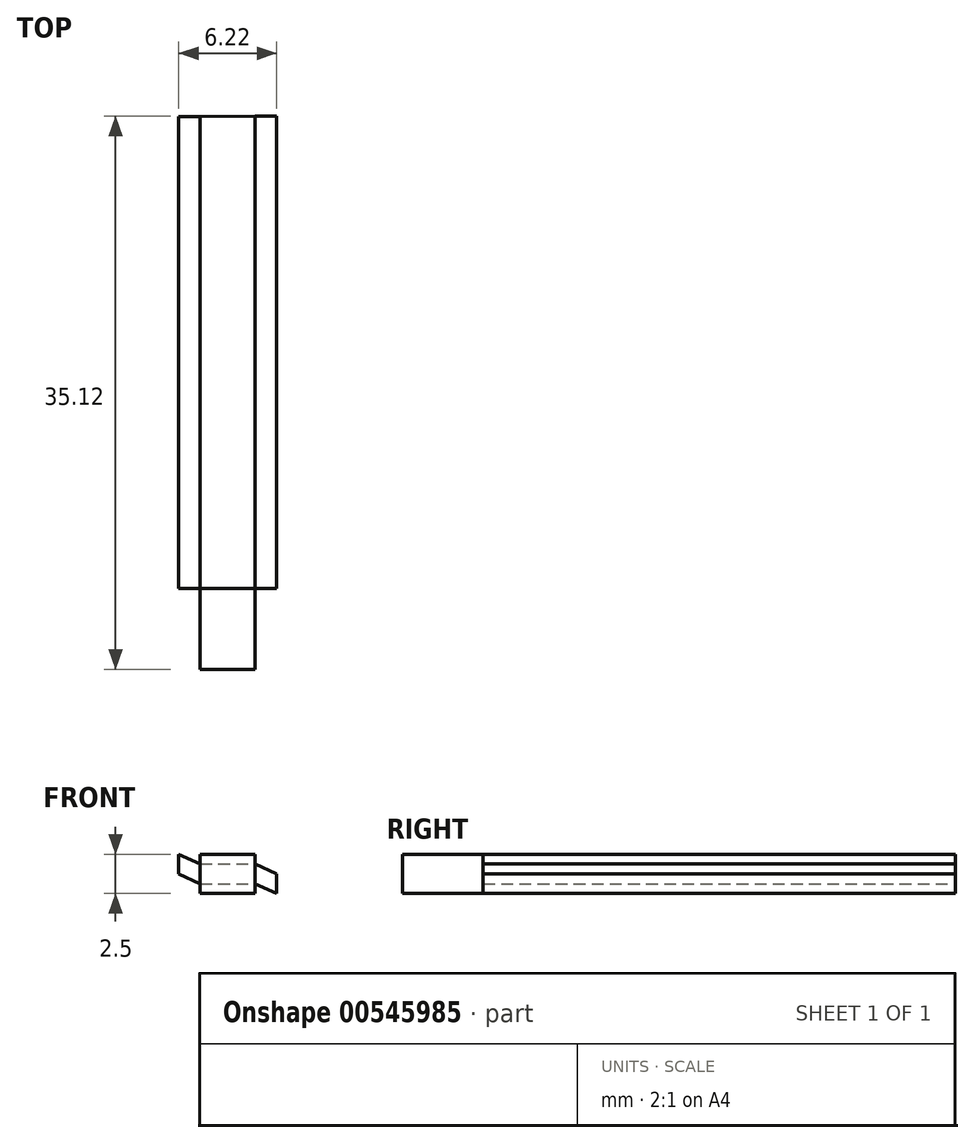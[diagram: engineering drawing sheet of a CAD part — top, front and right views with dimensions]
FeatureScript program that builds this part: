
annotation { "Feature Type Name" : "Feature", "Feature Type Description" : "" }
export const myFeature = defineFeature(function(context is Context, id is Id, definition is map)
    precondition{}
    {
        {
            var Q0;
            Q0=qCreatedBy(makeId("Top.planeOp"),FACE);
            var sketch = newSketch(context, id + "F0", { "sketchPlane" : qUnion([Q0])});
            skLineSegment(sketch, "E0", {"start": v(-3.25, 0) * mm, "end": v(3.25, 0) * mm});
            skLineSegment(sketch, "E1", {"start": v(-1.75, 0) * mm, "end": v(-1.75, -5.12) * mm});
            skLineSegment(sketch, "E2", {"start": v(-1.75, -5.12) * mm, "end": v(1.75, -5.12) * mm});
            skLineSegment(sketch, "E3", {"start": v(1.75, -5.12) * mm, "end": v(1.75, 0) * mm});
            skPoint(sketch, "E4", {"position": v(0, -5.12) * mm});
            skLineSegment(sketch, "E5", {"start": v(1.75, 0) * mm, "end": v(1.75, 30) * mm});
            skLineSegment(sketch, "E6", {"start": v(-1.75, 0) * mm, "end": v(-1.75, 29.98) * mm});
            skLineSegment(sketch, "E7", {"start": v(-1.75, 29.98) * mm, "end": v(1.75, 30) * mm});
            skSolve(sketch);
        }
        {
            var Q0;
            {var subQ2=sQuery(id+"F0.wireOp",EDGE,"E5");Q0=makeQuery(id+"F0.imprint","IMPRINT",FACE,{"disambiguationData":[TD([[makeQuery(id+"F0.imprint","IMPRINT",EDGE,{"derivedFrom":subQ2}),1.0]])]});}
            extrude(context, id + "F1", {"entities" : qUnion([Q0]), "depth" : 0.62 * mm, "offsetDistance" : 25 * mm, "hasSecondDirection" : true, "secondDirectionOppositeDirection" : true, "secondDirectionDepth" : 0.62 * mm});
        }
        {
            var Q0;
            Q0=qCreatedBy(makeId("Front.planeOp"),FACE);
            var sketch = newSketch(context, id + "F2", { "sketchPlane" : qUnion([Q0])});
            skLineSegment(sketch, "E8.bottom", {"start": v(-1.75, 0.64) * mm, "end": v(1.75, 0.64) * mm});
            skLineSegment(sketch, "E8.top", {"start": v(-1.75, -0.62) * mm, "end": v(1.75, -0.62) * mm});
            skLineSegment(sketch, "E8.left", {"start": v(-1.75, 0.64) * mm, "end": v(-1.75, -0.62) * mm});
            skLineSegment(sketch, "E8.right", {"start": v(1.75, 0.64) * mm, "end": v(1.75, -0.62) * mm});
            skLineSegment(sketch, "E9", {"start": v(-1.75, 0.64) * mm, "end": v(1.75, -0.62) * mm});
            skLineSegment(sketch, "E10", {"start": v(-1.75, 0.64) * mm, "end": v(-3.1, 1.26) * mm});
            skLineSegment(sketch, "E11", {"start": v(-3.1, 1.26) * mm, "end": v(-1.75, 1.26) * mm});
            skLineSegment(sketch, "E12", {"start": v(-1.75, 1.26) * mm, "end": v(-1.75, 0.64) * mm});
            skLineSegment(sketch, "E13", {"start": v(1.75, -0.62) * mm, "end": v(1.75, -1.25) * mm});
            skLineSegment(sketch, "E14", {"start": v(1.75, -1.25) * mm, "end": v(3.11, -1.25) * mm});
            skLineSegment(sketch, "E15", {"start": v(1.75, -0.62) * mm, "end": v(3.11, -1.25) * mm});
            skSolve(sketch);
        }
        {
            var Q0;
            Q0=makeQuery(id+"F1.opExtrude","SWEPT_FACE",FACE,{"disambiguationData":[OSD([sQuery(id+"F0.wireOp",EDGE,"E5")])]});
            var Q1;
            Q1=sQuery(id+"F2.wireOp",EDGE,"E15");
            sweep(context, id + "F3", {"operationType" : NewBodyOperationType.ADD, "profiles" : qUnion([Q0]), "path" : qUnion([Q1])});
        }
        {
            var Q0;
            Q0=makeQuery(id+"F1.opExtrude","SWEPT_FACE",FACE,{"disambiguationData":[OSD([sQuery(id+"F0.wireOp",EDGE,"E6")])]});
            var Q1;
            Q1=sQuery(id+"F2.wireOp",EDGE,"E10");
            sweep(context, id + "F4", {"operationType" : NewBodyOperationType.ADD, "profiles" : qUnion([Q0]), "path" : qUnion([Q1])});
        }
        {
            var Q0;
            {var subQ0=sQuery(id+"F0.wireOp",EDGE,"E1");Q0=makeQuery(id+"F0.imprint","IMPRINT",FACE,{"disambiguationData":[TD([[makeQuery(id+"F0.imprint","IMPRINT",EDGE,{"derivedFrom":subQ0}),1.0]])]});}
            extrude(context, id + "F5", {"entities" : qUnion([Q0]), "operationType" : NewBodyOperationType.ADD, "depth" : 1.25 * mm, "offsetDistance" : 25 * mm, "hasSecondDirection" : true, "secondDirectionOppositeDirection" : true, "secondDirectionDepth" : 1.25 * mm});
        }
    });
